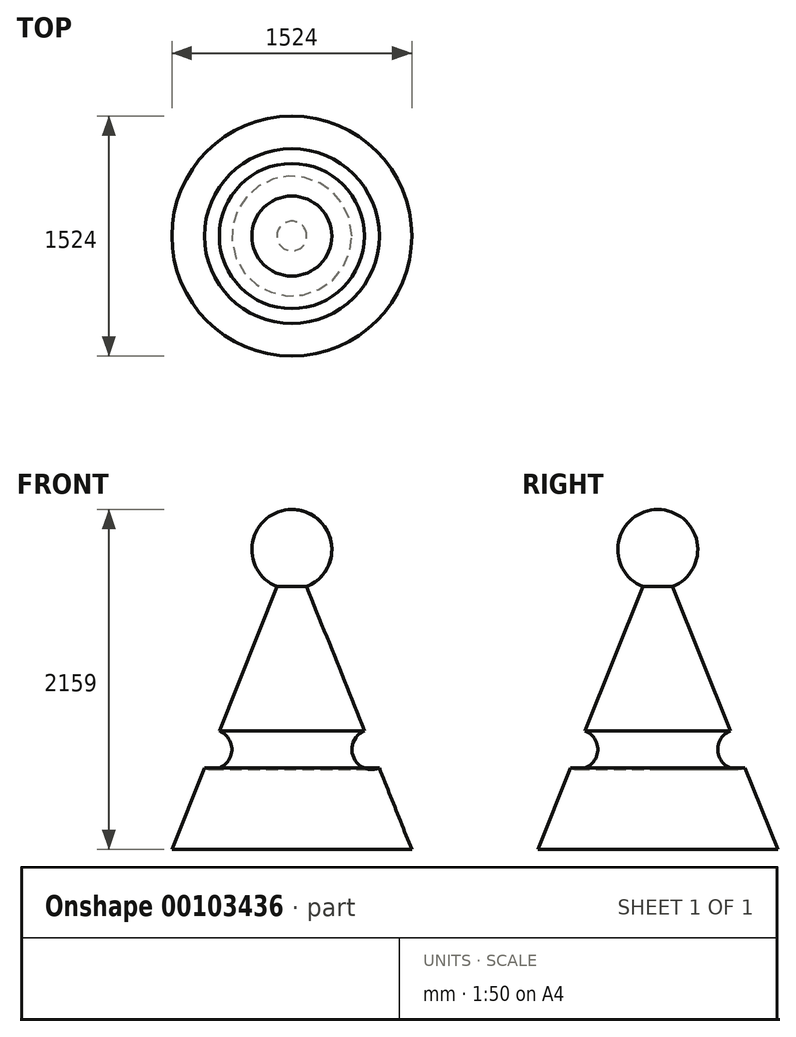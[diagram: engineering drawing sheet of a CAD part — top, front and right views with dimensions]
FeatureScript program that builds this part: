
annotation { "Feature Type Name" : "Feature", "Feature Type Description" : "" }
export const myFeature = defineFeature(function(context is Context, id is Id, definition is map)
    precondition{}
    {
        {
            var Q0;
            Q0=qCreatedBy(makeId("Front.planeOp"),FACE);
            var sketch = newSketch(context, id + "F0", { "sketchPlane" : qUnion([Q0])});
            skLineSegment(sketch, "E0", {"start": v(0, 1905) * mm, "end": v(0, -935.01) * mm, "construction": true});
            skArc(sketch, "E1", {"start": v(94.33, 1669.17) * mm, "mid": v(249.42, 1953.03) * mm, "end": v(0, 2159) * mm});
            skLineSegment(sketch, "E2", {"start": v(0, 2159) * mm, "end": v(0, 1651) * mm});
            skLineSegment(sketch, "E3", {"start": v(762, 0) * mm, "end": v(0, 0) * mm});
            skLineSegment(sketch, "E4", {"start": v(0, 2159) * mm, "end": v(0, 0) * mm});
            skLineSegment(sketch, "E5", {"start": v(94.33, 1669.17) * mm, "end": v(460.83, 752.92) * mm});
            skArc(sketch, "E6", {"start": v(460.83, 752.92) * mm, "mid": v(390.08, 587.83) * mm, "end": v(555.17, 517.08) * mm});
            skLineSegment(sketch, "E7.trimOffspring", {"start": v(555.17, 517.08) * mm, "end": v(762, 0) * mm});
            skSolve(sketch);
        }
        {
            var Q0;
            {var subQ1=sQuery(id+"F0.wireOp",EDGE,"E1");Q0=makeQuery(id+"F0.imprint","IMPRINT",FACE,{"disambiguationData":[TD([[makeQuery(id+"F0.imprint","IMPRINT",EDGE,{"derivedFrom":subQ1}),1.0]])]});}
            var Q1;
            Q1=sQuery(id+"F0.wireOp",EDGE,"E0");
            revolve(context, id + "F1", {"entities" : qUnion([Q0]), "axis" : qUnion([Q1]), "revolveType" : RevolveType.FULL});
        }
    });
